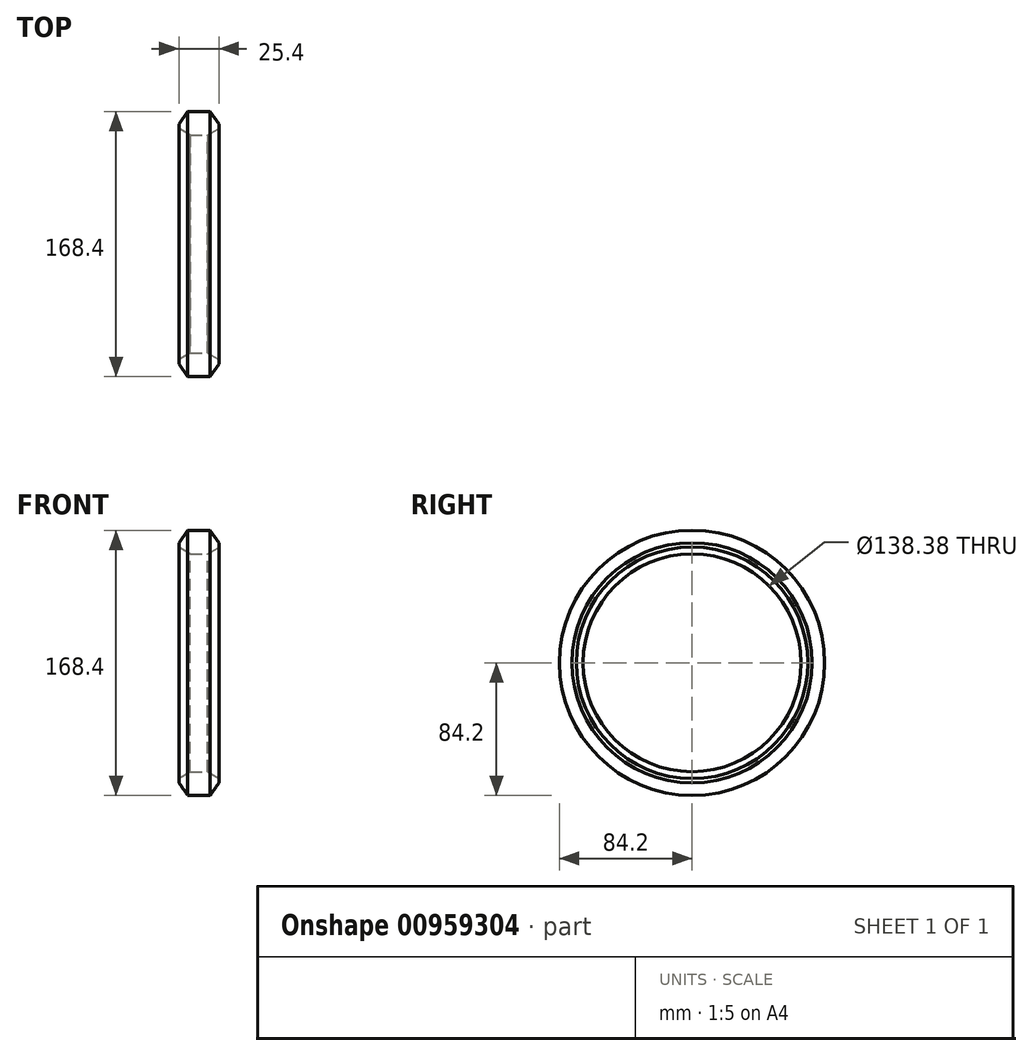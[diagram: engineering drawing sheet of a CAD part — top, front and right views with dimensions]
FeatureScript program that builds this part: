
annotation { "Feature Type Name" : "Feature", "Feature Type Description" : "" }
export const myFeature = defineFeature(function(context is Context, id is Id, definition is map)
    precondition{}
    {
        {
            var Q0;
            Q0=qCreatedBy(makeId("Front.planeOp"),FACE);
            var sketch = newSketch(context, id + "F0", { "sketchPlane" : qUnion([Q0])});
            skLineSegment(sketch, "E0", {"start": v(0, 0) * mm, "end": v(-129.88, 0) * mm, "construction": true});
            skLineSegment(sketch, "E1", {"start": v(0, 76.22) * mm, "end": v(0, 73.51) * mm});
            skLineSegment(sketch, "E2", {"start": v(0, 73.51) * mm, "end": v(-7.11, 69.19) * mm});
            skLineSegment(sketch, "E3", {"start": v(-7.11, 69.19) * mm, "end": v(-18.29, 69.19) * mm});
            skLineSegment(sketch, "E4", {"start": v(-18.29, 69.19) * mm, "end": v(-25.4, 73.51) * mm});
            skLineSegment(sketch, "E5", {"start": v(-25.4, 73.51) * mm, "end": v(-25.4, 76.22) * mm});
            skLineSegment(sketch, "E6", {"start": v(-25.4, 76.22) * mm, "end": v(-19.81, 84.2) * mm});
            skLineSegment(sketch, "E7", {"start": v(-19.81, 84.2) * mm, "end": v(-5.59, 84.2) * mm});
            skLineSegment(sketch, "E8", {"start": v(-5.59, 84.2) * mm, "end": v(0, 76.22) * mm});
            skSolve(sketch);
        }
        {
            var Q0;
            Q0=makeQuery(id+"F0.imprint","IMPRINT",FACE,{"disambiguationData":[TD([[makeQuery(id+"F0.imprint","IMPRINT",EDGE,{"derivedFrom":sQuery(id+"F0.wireOp",EDGE,"E1")}),-1.0]])]});
            var Q1;
            Q1=sQuery(id+"F0.wireOp",EDGE,"E0");
            revolve(context, id + "F1", {"surfaceOperationType" : NewSurfaceOperationType.NEW, "entities" : qUnion([Q0]), "axis" : qUnion([Q1]), "revolveType" : RevolveType.FULL});
        }
    });
